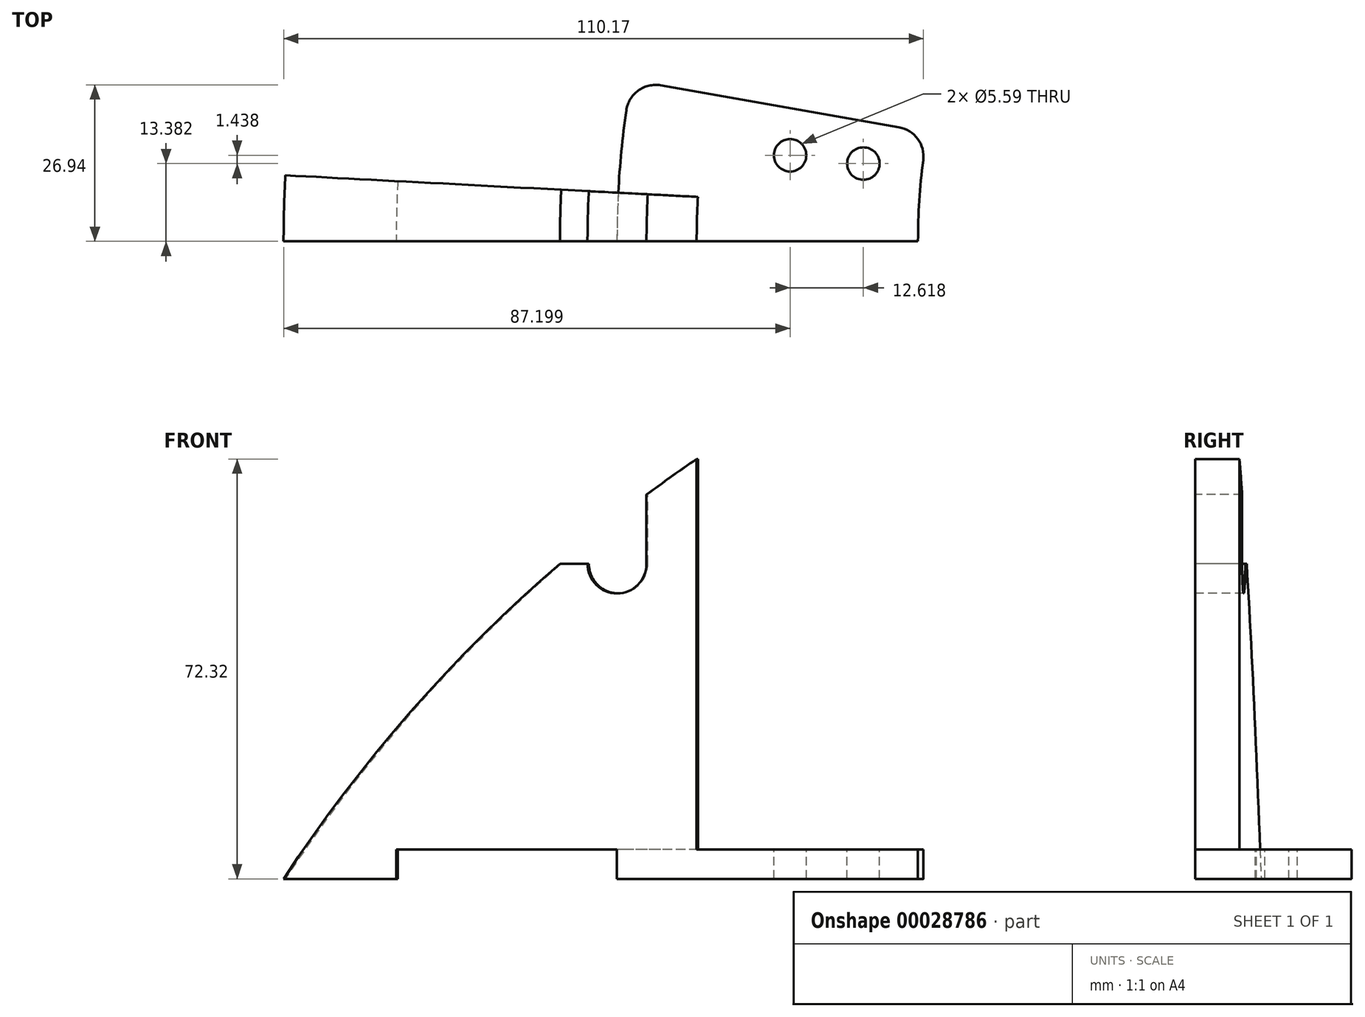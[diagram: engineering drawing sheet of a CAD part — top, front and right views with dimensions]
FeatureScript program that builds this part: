
annotation { "Feature Type Name" : "Feature", "Feature Type Description" : "" }
export const myFeature = defineFeature(function(context is Context, id is Id, definition is map)
    precondition{}
    {
        {
            var Q0;
            Q0=qCreatedBy(makeId("Front.planeOp"),FACE);
            var sketch = newSketch(context, id + "F0", { "sketchPlane" : qUnion([Q0])});
            skArc(sketch, "E0", {"start": v(228.6, 142.24) * mm, "mid": v(228.51, 142.38) * mm, "end": v(228.42, 142.53) * mm});
            skLineSegment(sketch, "E1", {"start": v(0, 269.24) * mm, "end": v(0, -269.24) * mm, "construction": true});
            skLineSegment(sketch, "E2", {"start": v(228.6, 142.53) * mm, "end": v(228.42, 142.53) * mm, "construction": true});
            skLineSegment(sketch, "E3", {"start": v(-279, 76.33) * mm, "end": v(507.36, 76.33) * mm, "construction": true});
            skLineSegment(sketch, "E4", {"start": v(-228.42, 142.53) * mm, "end": v(-228.42, 76.33) * mm, "construction": true});
            skLineSegment(sketch, "E5", {"start": v(-254, 174.53) * mm, "end": v(-254, 8.55) * mm, "construction": true});
            skLineSegment(sketch, "E6", {"start": v(-228.42, 142.53) * mm, "end": v(-254, 76.33) * mm});
            skLineSegment(sketch, "E7", {"start": v(-217.27, 142.53) * mm, "end": v(217.27, 142.53) * mm, "construction": true});
            skArc(sketch, "E8.trimOffspring", {"start": v(254, 54.82) * mm, "mid": v(251.42, 65.63) * mm, "end": v(248.38, 76.33) * mm});
            skArc(sketch, "E9.trimOffspring", {"start": v(0, 259.85) * mm, "mid": v(-123.46, 228.64) * mm, "end": v(-217.27, 142.53) * mm});
            skLineSegment(sketch, "E10", {"start": v(-217.27, 142.53) * mm, "end": v(-242.85, 76.33) * mm});
            skLineSegment(sketch, "E11", {"start": v(-254, 76.33) * mm, "end": v(-242.85, 76.33) * mm});
            skLineSegment(sketch, "E12", {"start": v(0, 269.24) * mm, "end": v(0, 259.85) * mm});
            skPoint(sketch, "E13.end.orphan", {"position": v(243.42, 76.33) * mm});
            skPoint(sketch, "E14.orphan", {"position": v(232.09, 76.33) * mm});
            skArc(sketch, "E15.trimOffspring", {"start": v(0, 269.24) * mm, "mid": v(-130.6, 235.44) * mm, "end": v(-228.42, 142.53) * mm});
            skLineSegment(sketch, "E16.trimOffspring", {"start": v(0, 142.53) * mm, "end": v(-228.42, 142.53) * mm, "construction": true});
            skLineSegment(sketch, "E17", {"start": v(0, 259.85) * mm, "end": v(-183.52, 76.33) * mm, "construction": true});
            skLineSegment(sketch, "E18", {"start": v(-217.27, 142.53) * mm, "end": v(-217.27, 266.7) * mm, "construction": true});
            skLineSegment(sketch, "E19", {"start": v(-146.15, 142.53) * mm, "end": v(-146.15, 289.46) * mm, "construction": true});
            skLineSegment(sketch, "E20", {"start": v(-252.15, 215.8) * mm, "end": v(47.32, 215.8) * mm, "construction": true});
            skLineSegment(sketch, "E21", {"start": v(-146.15, 142.53) * mm, "end": v(-146.15, 214.85) * mm});
            skLineSegment(sketch, "E22", {"start": v(-159.87, 142.53) * mm, "end": v(-159.87, 250.26) * mm, "construction": true});
            skLineSegment(sketch, "E23", {"start": v(-244.24, 196.78) * mm, "end": v(-117.26, 196.78) * mm, "construction": true});
            skCircle(sketch, "E24", {"center": v(-159.87, 196.78) * mm, "radius": 5.08 * mm});
            skLineSegment(sketch, "E25", {"start": v(-154.79, 196.78) * mm, "end": v(-154.79, 208.71) * mm});
            skLineSegment(sketch, "E26", {"start": v(-164.95, 196.78) * mm, "end": v(-169.7, 196.78) * mm});
            skLineSegment(sketch, "E27", {"start": v(-228.42, 142.53) * mm, "end": v(-146.15, 142.53) * mm});
            skLineSegment(sketch, "E28", {"start": v(-146.15, 142.53) * mm, "end": v(-146.15, 226.12) * mm});
            skLineSegment(sketch, "E29.bottom", {"start": v(-159.87, 142.53) * mm, "end": v(-197.88, 142.53) * mm});
            skLineSegment(sketch, "E29.top", {"start": v(-159.87, 147.6) * mm, "end": v(-197.88, 147.6) * mm});
            skLineSegment(sketch, "E29.left", {"start": v(-159.87, 142.53) * mm, "end": v(-159.87, 147.6) * mm});
            skLineSegment(sketch, "E29.right", {"start": v(-197.88, 142.53) * mm, "end": v(-197.88, 147.6) * mm});
            skLineSegment(sketch, "E30", {"start": v(-217.27, 142.53) * mm, "end": v(-120.38, 258) * mm, "construction": true});
            skLineSegment(sketch, "E31", {"start": v(-108.05, 119.31) * mm, "end": v(-108.05, 234.69) * mm, "construction": true});
            skLineSegment(sketch, "E32.bottom", {"start": v(-108.05, 142.53) * mm, "end": v(-159.87, 142.53) * mm});
            skLineSegment(sketch, "E32.top", {"start": v(-108.05, 147.6) * mm, "end": v(-159.87, 147.6) * mm});
            skLineSegment(sketch, "E32.left", {"start": v(-108.05, 142.53) * mm, "end": v(-108.05, 147.6) * mm});
            skLineSegment(sketch, "E33.bottom", {"start": v(-108.05, 147.6) * mm, "end": v(-146.15, 147.6) * mm});
            skLineSegment(sketch, "E33.top", {"start": v(-108.05, 158.4) * mm, "end": v(-146.15, 158.4) * mm});
            skLineSegment(sketch, "E33.left", {"start": v(-108.05, 147.6) * mm, "end": v(-108.05, 158.4) * mm});
            skLineSegment(sketch, "E33.right", {"start": v(-146.15, 147.6) * mm, "end": v(-146.15, 158.4) * mm});
            skSolve(sketch);
        }
        {
            var Q0;
            {var subQ0=sQuery(id+"F0.wireOp",EDGE,"E25");Q0=makeQuery(id+"F0.imprint","IMPRINT",FACE,{"disambiguationData":[TD([[makeQuery(id+"F0.imprint","IMPRINT",EDGE,{"derivedFrom":subQ0}),-1.0]])]});}
            var Q1;
            Q1=makeQuery(id+"F0.imprint","IMPRINT",FACE,{"disambiguationData":[TD([[makeQuery(id+"F0.imprint","IMPRINT",EDGE,{"derivedFrom":sQuery(id+"F0.wireOp",EDGE,"E29.bottom")}),-1.0]])]});
            var Q2;
            Q2=makeQuery(id+"F0.imprint","IMPRINT",FACE,{"disambiguationData":[TD([[makeQuery(id+"F0.imprint","IMPRINT",EDGE,{"derivedFrom":sQuery(id+"F0.wireOp",EDGE,"E33.bottom")}),-1.0]])]});
            var Q3;
            Q3=sQuery(id+"F0.wireOp",EDGE,"E1");
            revolve(context, id + "F1", {"entities" : qUnion([Q0, Q1, Q2]), "axis" : qUnion([Q3]), "revolveType" : RevolveType.ONE_DIRECTION, "angle" : 3 * degree});
        }
        {
            var Q0;
            {var subQ5=sQuery(id+"F0.wireOp",EDGE,"E32.left");Q0=makeQuery(id+"F0.imprint","IMPRINT",FACE,{"disambiguationData":[TD([[makeQuery(id+"F0.imprint","IMPRINT",EDGE,{"derivedFrom":subQ5}),1.0]])]});}
            var Q1;
            {var subQ5=sQuery(id+"F0.wireOp",EDGE,"E29.left");Q1=makeQuery(id+"F0.imprint","IMPRINT",FACE,{"disambiguationData":[TD([[makeQuery(id+"F0.imprint","IMPRINT",EDGE,{"derivedFrom":subQ5}),-1.0]])]});}
            var Q2;
            Q2=sQuery(id+"F0.wireOp",EDGE,"E1");
            revolve(context, id + "F2", {"operationType" : NewBodyOperationType.ADD, "entities" : qUnion([Q0, Q1]), "axis" : qUnion([Q2]), "revolveType" : RevolveType.ONE_DIRECTION, "angle" : 10 * degree});
        }
        {
            var Q0;
            Q0=makeQuery(id+"F2.opRevolve","SWEPT_FACE",FACE,{"disambiguationData":[OSD([sQuery(id+"F0.wireOp",EDGE,"E32.top"),sQuery(id+"F0.wireOp",EDGE,"E33.bottom")])]});
            var sketch = newSketch(context, id + "F3", { "sketchPlane" : qUnion([Q0])});
            skLineSegment(sketch, "E34", {"start": v(-158.84, 18.1) * mm, "end": v(-107.36, 12.23) * mm, "construction": true});
            skCircle(sketch, "E35", {"center": v(-130.07, 14.82) * mm, "radius": 2.8 * mm});
            skCircle(sketch, "E36", {"center": v(-117.45, 13.38) * mm, "radius": 2.8 * mm});
            skSolve(sketch);
        }
        {
            var Q0;
            Q0=makeQuery(id+"F3.imprint","IMPRINT",FACE,{"disambiguationData":[TD([[makeQuery(id+"F3.imprint","IMPRINT",EDGE,{"derivedFrom":sQuery(id+"F3.wireOp",EDGE,"E35")}),1.0]])]});
            var Q1;
            Q1=makeQuery(id+"F3.imprint","IMPRINT",FACE,{"disambiguationData":[TD([[makeQuery(id+"F3.imprint","IMPRINT",EDGE,{"derivedFrom":sQuery(id+"F3.wireOp",EDGE,"E36")}),1.0]])]});
            extrude(context, id + "F4", {"entities" : qUnion([Q0, Q1]), "operationType" : NewBodyOperationType.REMOVE, "oppositeDirection" : true, "depth" : 25.4 * mm});
        }
        {
            var Q0;
            Q0=makeQuery(id+"F1.opRevolve","SWEPT_EDGE",EDGE,{"disambiguationData":[OSD([sQuery(id+"F0.wireOp",EDGE,"E33.top"),sQuery(id+"F0.wireOp",EDGE,"E33.left")])]});
            var Q1;
            Q1=makeQuery(id+"F2.opRevolve","CAP_EDGE",EDGE,{"disambiguationData":[OSD([sQuery(id+"F0.wireOp",EDGE,"E32.left")])],"isStart":false});
            var Q2;
            Q2=makeQuery(id+"F2.opRevolve","CAP_EDGE",EDGE,{"disambiguationData":[OSD([sQuery(id+"F0.wireOp",EDGE,"E29.left")])],"isStart":false});
            fillet(context, id + "F5", {"entities" : qUnion([Q0, Q1, Q2]), "radius" : 5.08 * mm, "tangentPropagation" : true, "allowEdgeOverflow" : false});
        }
    });
